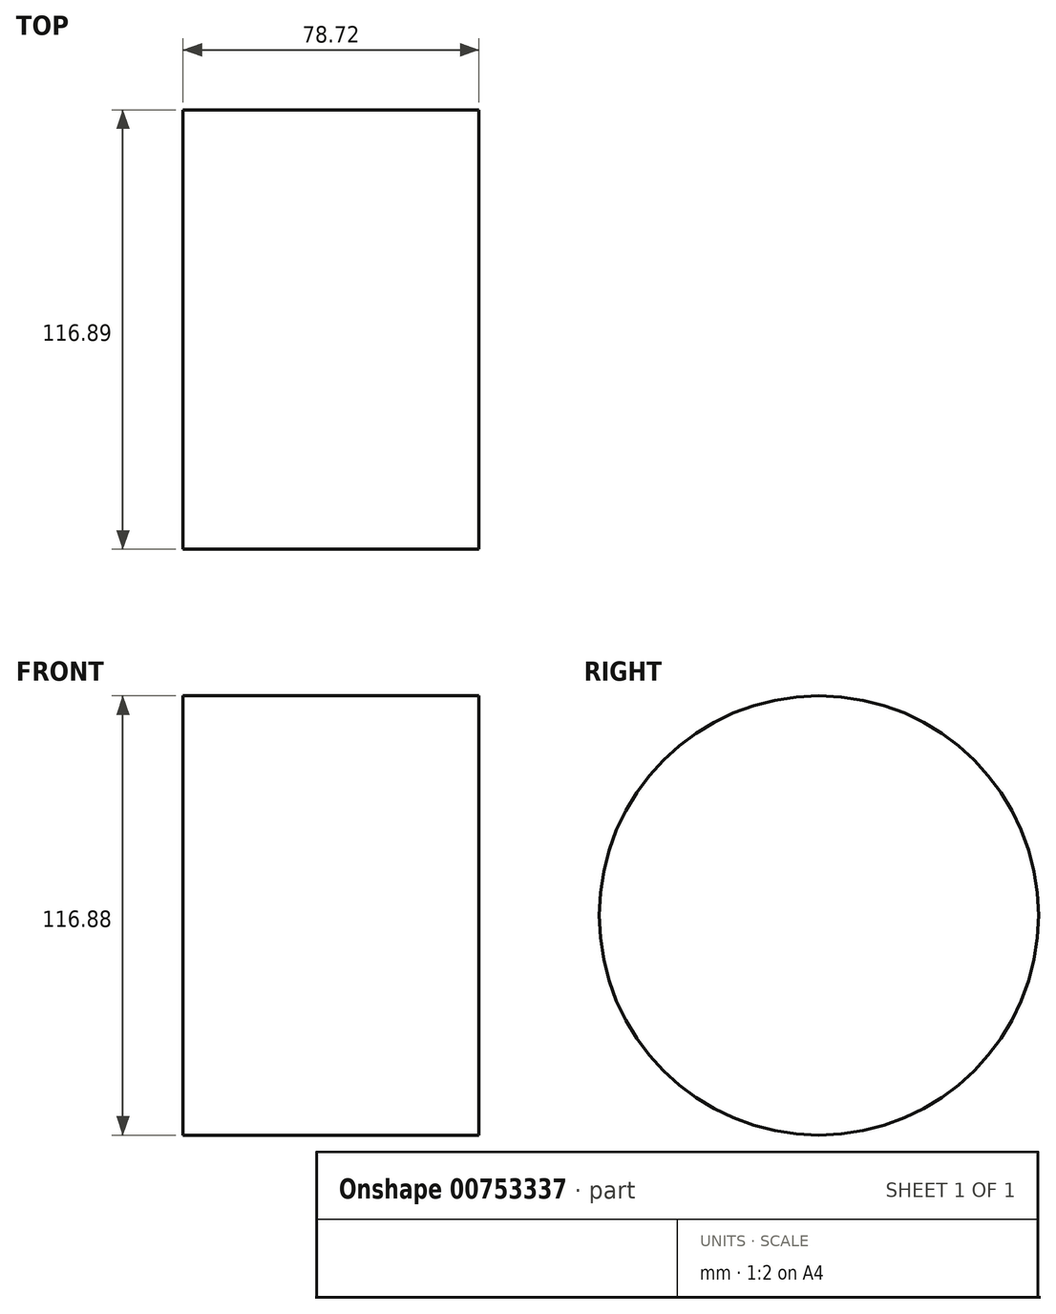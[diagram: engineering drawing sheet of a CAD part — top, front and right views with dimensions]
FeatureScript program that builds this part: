
annotation { "Feature Type Name" : "Feature", "Feature Type Description" : "" }
export const myFeature = defineFeature(function(context is Context, id is Id, definition is map)
    precondition{}
    {
        {
            var Q0;
            Q0=qCreatedBy(makeId("Top.planeOp"),FACE);
            var sketch = newSketch(context, id + "F0", { "sketchPlane" : qUnion([Q0])});
            skLineSegment(sketch, "E0.bottom", {"start": v(-41.56, 27.6) * mm, "end": v(37.16, 27.6) * mm});
            skLineSegment(sketch, "E0.top", {"start": v(-41.56, -30.84) * mm, "end": v(37.16, -30.84) * mm});
            skLineSegment(sketch, "E0.left", {"start": v(-41.56, 27.6) * mm, "end": v(-41.56, -30.84) * mm});
            skLineSegment(sketch, "E0.right", {"start": v(37.16, 27.6) * mm, "end": v(37.16, -30.84) * mm});
            skSolve(sketch);
        }
        {
            var Q0;
            Q0=makeQuery(id+"F0.imprint","IMPRINT",FACE,{"disambiguationData":[TD([[makeQuery(id+"F0.imprint","IMPRINT",EDGE,{"derivedFrom":sQuery(id+"F0.wireOp",EDGE,"E0.bottom")}),-1.0]])]});
            var Q1;
            Q1=sQuery(id+"F0.wireOp",EDGE,"E0.top");
            revolve(context, id + "F1", {"surfaceOperationType" : NewSurfaceOperationType.NEW, "entities" : qUnion([Q0]), "axis" : qUnion([Q1]), "revolveType" : RevolveType.FULL});
        }
    });
